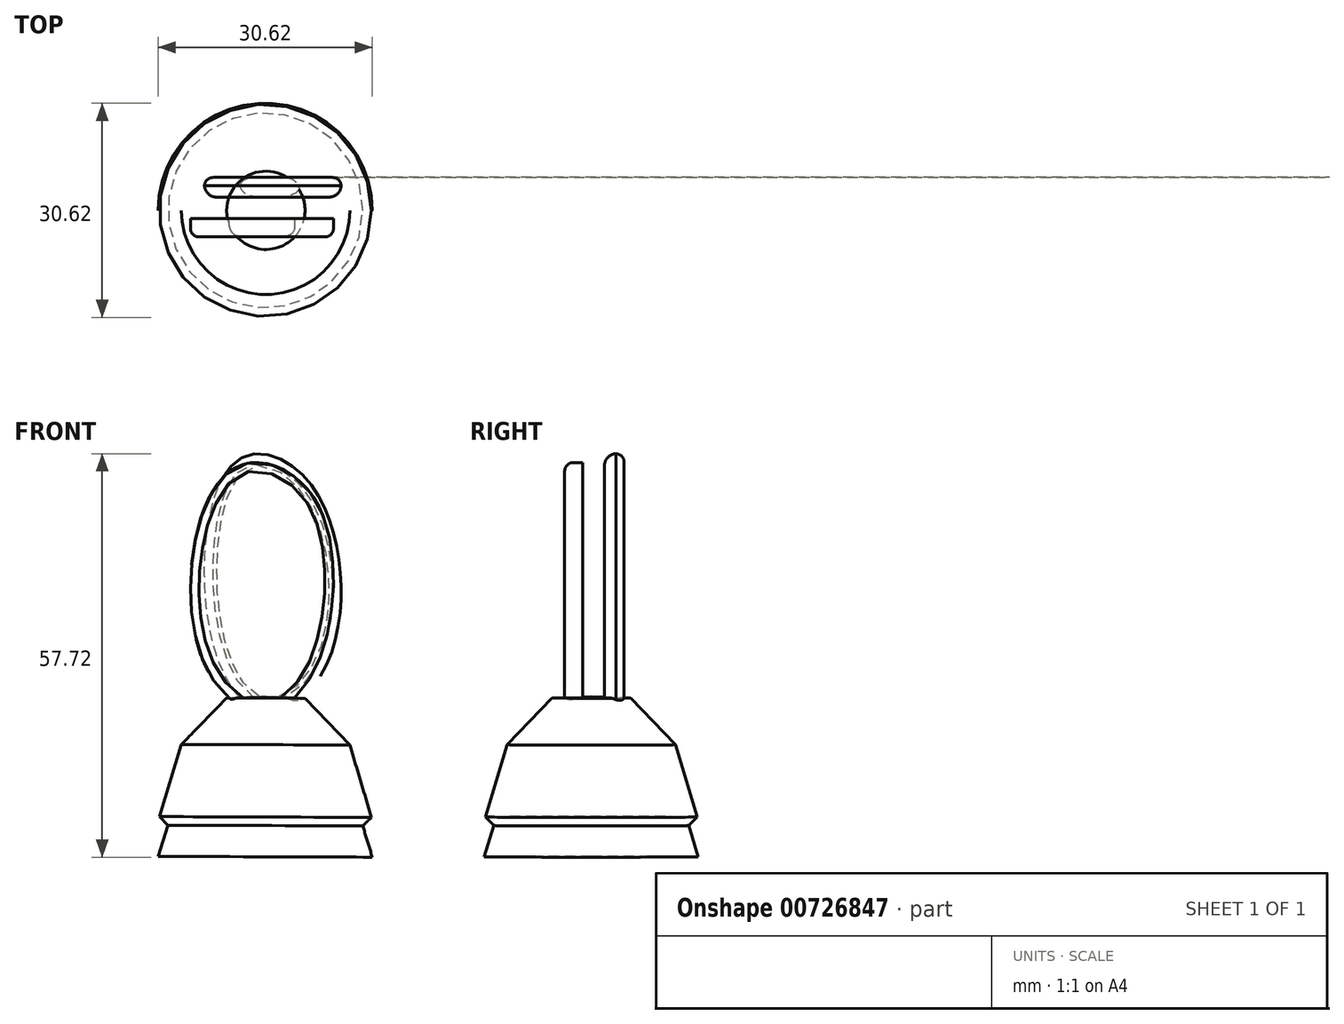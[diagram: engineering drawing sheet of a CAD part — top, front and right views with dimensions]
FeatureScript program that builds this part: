
annotation { "Feature Type Name" : "Feature", "Feature Type Description" : "" }
export const myFeature = defineFeature(function(context is Context, id is Id, definition is map)
    precondition{}
    {
        {
            var Q0;
            Q0=qCreatedBy(makeId("Front.planeOp"),FACE);
            var sketch = newSketch(context, id + "F0", { "sketchPlane" : qUnion([Q0])});
            skLineSegment(sketch, "E0", {"start": v(0, 0) * mm, "end": v(-15.31, 0) * mm});
            skLineSegment(sketch, "E1", {"start": v(-15.31, 0) * mm, "end": v(-13.91, 4.46) * mm});
            skLineSegment(sketch, "E2", {"start": v(-13.91, 4.46) * mm, "end": v(-15.14, 5.69) * mm});
            skLineSegment(sketch, "E3", {"start": v(-15.14, 5.69) * mm, "end": v(-11.99, 16.01) * mm});
            skLineSegment(sketch, "E4", {"start": v(-11.99, 16.01) * mm, "end": v(-5.51, 22.66) * mm});
            skLineSegment(sketch, "E5", {"start": v(-5.51, 22.66) * mm, "end": v(0.09, 22.84) * mm});
            skLineSegment(sketch, "E6", {"start": v(0.09, 22.84) * mm, "end": v(0, 0) * mm});
            skSolve(sketch);
        }
        {
            var Q0;
            Q0=makeQuery(id+"F0.imprint","IMPRINT",FACE,{"disambiguationData":[TD([[makeQuery(id+"F0.imprint","IMPRINT",EDGE,{"derivedFrom":sQuery(id+"F0.wireOp",EDGE,"E0")}),-1.0]])]});
            var Q1;
            Q1=sQuery(id+"F0.wireOp",EDGE,"E6");
            revolve(context, id + "F1", {"surfaceOperationType" : NewSurfaceOperationType.NEW, "entities" : qUnion([Q0]), "axis" : qUnion([Q1]), "revolveType" : RevolveType.FULL});
        }
        {
            var Q0;
            Q0=qCreatedBy(makeId("Front.planeOp"),FACE);
            cPlane(context, id + "F2", {"entities" : qUnion([Q0]), "cplaneType" : CPlaneType.OFFSET, "offset" : 3.8 * mm, "width" : 150 * mm, "height" : 150 * mm});
        }
        {
            var Q0;
            Q0=qCreatedBy(id+"F2.planeOp",FACE);
            var sketch = newSketch(context, id + "F3", { "sketchPlane" : qUnion([Q0])});
            skFitSpline(sketch, "E7", {"points": [v(-2.85, 56.15) * mm, v(-9.6, 47.04) * mm, v(-8.67, 27.46) * mm, v(-0.58, 20.66) * mm, v(7.41, 27.4) * mm, v(7.33, 50.68) * mm, v(-2.85, 56.15) * mm]});
            skSolve(sketch);
        }
        {
            var Q0;
            Q0=makeQuery(id+"F3.imprint","IMPRINT",FACE,{"disambiguationData":[TD([[makeQuery(id+"F3.imprint","IMPRINT",EDGE,{"derivedFrom":sQuery(id+"F3.wireOp",EDGE,"E7")}),1.0]])]});
            extrude(context, id + "F4", {"entities" : qUnion([Q0]), "operationType" : NewBodyOperationType.ADD, "oppositeDirection" : true, "depth" : 2.6 * mm, "offsetDistance" : 25 * mm});
        }
        {
            var Q0;
            Q0=makeQuery(id+"F4.opExtrude","CAP_EDGE",EDGE,{"disambiguationData":[OSD([sQuery(id+"F3.wireOp",EDGE,"E7")])],"isStart":true});
            fillet(context, id + "F5", {"entities" : qUnion([Q0]), "radius" : 1.2 * mm, "tangentPropagation" : true, "allowEdgeOverflow" : false});
        }
        {
            var Q0;
            Q0=qCreatedBy(makeId("Front.planeOp"),FACE);
            cPlane(context, id + "F6", {"entities" : qUnion([Q0]), "cplaneType" : CPlaneType.OFFSET, "offset" : 4.7 * mm, "oppositeDirection" : true, "width" : 150 * mm, "height" : 150 * mm});
        }
        {
            var Q0;
            Q0=qCreatedBy(id+"F6.planeOp",FACE);
            var sketch = newSketch(context, id + "F7", { "sketchPlane" : qUnion([Q0])});
            skFitSpline(sketch, "E8", {"points": [v(-3.76, 56.79) * mm, v(7.09, 52.41) * mm, v(8.66, 27.21) * mm, v(-0.96, 21.09) * mm, v(-8.31, 34.91) * mm, v(-3.76, 56.79) * mm]});
            skSolve(sketch);
        }
        {
            var Q0;
            Q0=makeQuery(id+"F7.imprint","IMPRINT",FACE,{"disambiguationData":[TD([[makeQuery(id+"F7.imprint","IMPRINT",EDGE,{"derivedFrom":sQuery(id+"F7.wireOp",EDGE,"E8")}),-1.0]])]});
            extrude(context, id + "F8", {"entities" : qUnion([Q0]), "operationType" : NewBodyOperationType.ADD, "depth" : 2.8 * mm, "offsetDistance" : 25 * mm});
        }
        {
            var Q0;
            Q0=makeQuery(id+"F8.opExtrude","CAP_EDGE",EDGE,{"disambiguationData":[OSD([sQuery(id+"F7.wireOp",EDGE,"E8")])],"isStart":true});
            fillet(context, id + "F9", {"entities" : qUnion([Q0]), "radius" : 1.2 * mm, "tangentPropagation" : true, "allowEdgeOverflow" : false});
        }
        {
            var Q0;
            Q0=makeQuery(id+"F8.opExtrude","CAP_EDGE",EDGE,{"disambiguationData":[OSD([sQuery(id+"F7.wireOp",EDGE,"E8")])],"isStart":false});
            fillet(context, id + "F10", {"entities" : qUnion([Q0]), "radius" : 1.69 * mm, "tangentPropagation" : true, "allowEdgeOverflow" : false});
        }
    });
